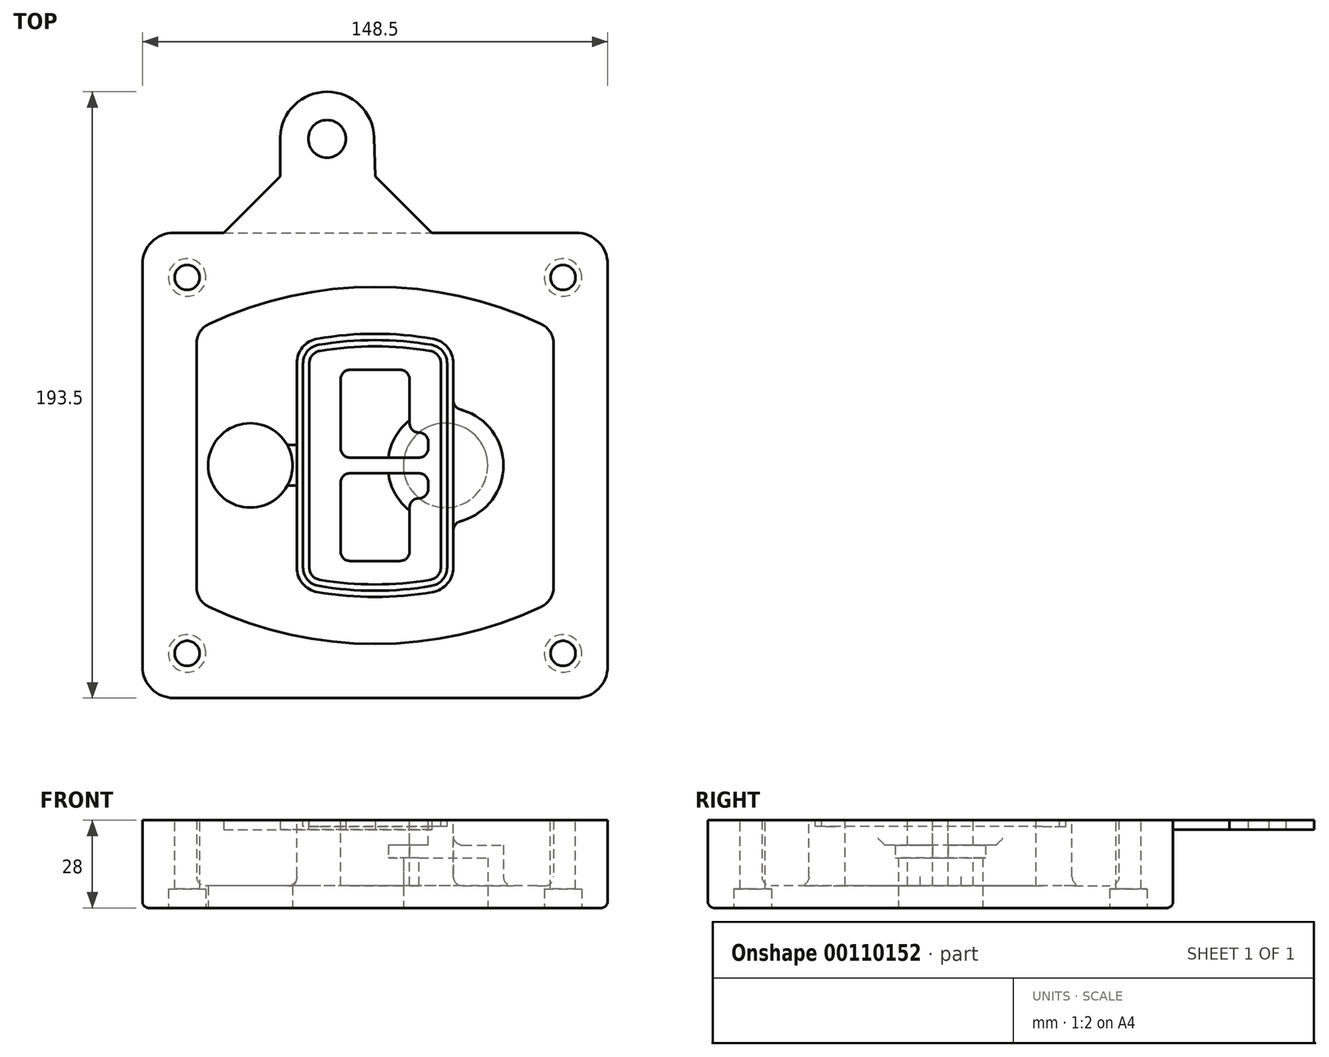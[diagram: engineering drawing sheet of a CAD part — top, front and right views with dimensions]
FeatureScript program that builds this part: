
annotation { "Feature Type Name" : "Feature", "Feature Type Description" : "" }
export const myFeature = defineFeature(function(context is Context, id is Id, definition is map)
    precondition{}
    {
        {
            var Q0;
            Q0=qCreatedBy(makeId("Top.planeOp"),FACE);
            var sketch = newSketch(context, id + "F0", { "sketchPlane" : qUnion([Q0])});
            skPoint(sketch, "E0.rect.middle", {"position": v(0, 0) * mm});
            skLineSegment(sketch, "E1.bottom", {"start": v(-64.25, -74.25) * mm, "end": v(64.25, -74.25) * mm});
            skLineSegment(sketch, "E1.top", {"start": v(-64.25, 74.25) * mm, "end": v(64.25, 74.25) * mm});
            skLineSegment(sketch, "E1.left", {"start": v(-74.25, -64.25) * mm, "end": v(-74.25, 64.25) * mm});
            skLineSegment(sketch, "E1.right", {"start": v(74.25, -64.25) * mm, "end": v(74.25, 64.25) * mm});
            skLineSegment(sketch, "E2", {"start": v(-74.25, 74.25) * mm, "end": v(74.25, -74.25) * mm, "construction": true});
            skLineSegment(sketch, "E3", {"start": v(74.25, 74.25) * mm, "end": v(-74.25, -74.25) * mm, "construction": true});
            skCircle(sketch, "E4", {"center": v(-60, 60) * mm, "radius": 4 * mm});
            skCircle(sketch, "E5", {"center": v(60, 60) * mm, "radius": 4 * mm});
            skCircle(sketch, "E6", {"center": v(60, -60) * mm, "radius": 4 * mm});
            skCircle(sketch, "E7", {"center": v(-60, -60) * mm, "radius": 4 * mm});
            skLineSegment(sketch, "E8", {"start": v(-60, 60) * mm, "end": v(60, 60) * mm, "construction": true});
            skLineSegment(sketch, "E9", {"start": v(60, 60) * mm, "end": v(60, -60) * mm, "construction": true});
            skLineSegment(sketch, "E10", {"start": v(60, -60) * mm, "end": v(-60, -60) * mm, "construction": true});
            skLineSegment(sketch, "E11", {"start": v(-60, -60) * mm, "end": v(-60, 60) * mm, "construction": true});
            skLineSegment(sketch, "E12", {"start": v(-60, 38.83) * mm, "end": v(-60, -38.83) * mm});
            skLineSegment(sketch, "E13", {"start": v(60, 38.83) * mm, "end": v(60, -38.83) * mm});
            skArc(sketch, "E14", {"start": v(54.26, 47.88) * mm, "mid": v(0, 60) * mm, "end": v(-54.26, 47.88) * mm});
            skArc(sketch, "E15", {"start": v(-54.26, -47.88) * mm, "mid": v(0, -60) * mm, "end": v(54.26, -47.88) * mm});
            skLineSegment(sketch, "E16", {"start": v(-60, 0) * mm, "end": v(60, 0) * mm, "construction": true});
            skPoint(sketch, "E17.visualSharp", {"position": v(-60, -45) * mm});
            skArc(sketch, "E17.filletArc", {"start": v(-60, -38.83) * mm, "mid": v(-58.44, -44.2) * mm, "end": v(-54.26, -47.88) * mm});
            skPoint(sketch, "E18.visualSharp", {"position": v(-60, 45) * mm});
            skArc(sketch, "E18.filletArc", {"start": v(-54.26, 47.88) * mm, "mid": v(-58.44, 44.2) * mm, "end": v(-60, 38.83) * mm});
            skPoint(sketch, "E19.visualSharp", {"position": v(60, 45) * mm});
            skArc(sketch, "E19.filletArc", {"start": v(60, 38.83) * mm, "mid": v(58.44, 44.2) * mm, "end": v(54.26, 47.88) * mm});
            skPoint(sketch, "E20.visualSharp", {"position": v(60, -45) * mm});
            skArc(sketch, "E20.filletArc", {"start": v(54.26, -47.88) * mm, "mid": v(58.44, -44.2) * mm, "end": v(60, -38.83) * mm});
            skPoint(sketch, "E21.visualSharp", {"position": v(-74.25, 74.25) * mm});
            skArc(sketch, "E21.filletArc", {"start": v(-64.25, 74.25) * mm, "mid": v(-71.32, 71.32) * mm, "end": v(-74.25, 64.25) * mm});
            skPoint(sketch, "E22.visualSharp", {"position": v(74.25, 74.25) * mm});
            skArc(sketch, "E22.filletArc", {"start": v(74.25, 64.25) * mm, "mid": v(71.32, 71.32) * mm, "end": v(64.25, 74.25) * mm});
            skPoint(sketch, "E23.visualSharp", {"position": v(74.25, -74.25) * mm});
            skArc(sketch, "E23.filletArc", {"start": v(64.25, -74.25) * mm, "mid": v(71.32, -71.32) * mm, "end": v(74.25, -64.25) * mm});
            skPoint(sketch, "E24.visualSharp", {"position": v(-74.25, -74.25) * mm});
            skArc(sketch, "E24.filletArc", {"start": v(-74.25, -64.25) * mm, "mid": v(-71.32, -71.32) * mm, "end": v(-64.25, -74.25) * mm});
            skArc(sketch, "E25.0", {"start": v(57, 38.83) * mm, "mid": v(55.9, 42.58) * mm, "end": v(52.98, 45.17) * mm});
            skLineSegment(sketch, "E25.1", {"start": v(57, 38.83) * mm, "end": v(57, -38.83) * mm});
            skArc(sketch, "E25.2", {"start": v(52.98, -45.17) * mm, "mid": v(55.9, -42.58) * mm, "end": v(57, -38.83) * mm});
            skArc(sketch, "E25.3", {"start": v(-52.98, -45.17) * mm, "mid": v(0, -57) * mm, "end": v(52.98, -45.17) * mm});
            skArc(sketch, "E25.4", {"start": v(-57, -38.83) * mm, "mid": v(-55.9, -42.58) * mm, "end": v(-52.98, -45.17) * mm});
            skArc(sketch, "E25.5", {"start": v(52.98, 45.17) * mm, "mid": v(0, 57) * mm, "end": v(-52.98, 45.17) * mm});
            skLineSegment(sketch, "E25.6", {"start": v(-57, 38.83) * mm, "end": v(-57, -38.83) * mm});
            skArc(sketch, "E25.7", {"start": v(-52.98, 45.17) * mm, "mid": v(-55.9, 42.58) * mm, "end": v(-57, 38.83) * mm});
            skArc(sketch, "E26.0", {"start": v(-55.96, 51.5) * mm, "mid": v(-61.82, 46.33) * mm, "end": v(-64, 38.83) * mm});
            skArc(sketch, "E26.1", {"start": v(55.96, 51.5) * mm, "mid": v(0, 64) * mm, "end": v(-55.96, 51.5) * mm});
            skArc(sketch, "E26.2", {"start": v(64, 38.83) * mm, "mid": v(61.82, 46.33) * mm, "end": v(55.96, 51.5) * mm});
            skLineSegment(sketch, "E26.3", {"start": v(64, 38.83) * mm, "end": v(64, -38.83) * mm});
            skArc(sketch, "E26.4", {"start": v(55.96, -51.5) * mm, "mid": v(61.82, -46.33) * mm, "end": v(64, -38.83) * mm});
            skLineSegment(sketch, "E26.5", {"start": v(-64, 38.83) * mm, "end": v(-64, -38.83) * mm});
            skArc(sketch, "E26.6", {"start": v(-55.96, -51.5) * mm, "mid": v(0, -64) * mm, "end": v(55.96, -51.5) * mm});
            skArc(sketch, "E26.7", {"start": v(-64, -38.83) * mm, "mid": v(-61.82, -46.33) * mm, "end": v(-55.96, -51.5) * mm});
            skSolve(sketch);
        }
        {
            var Q0;
            Q0=makeQuery(id+"F0.imprint","IMPRINT",FACE,{"disambiguationData":[TD([[makeQuery(id+"F0.imprint","IMPRINT",EDGE,{"derivedFrom":sQuery(id+"F0.wireOp",EDGE,"E1.bottom")}),1.0]])]});
            var Q1;
            Q1=makeQuery(id+"F0.imprint","IMPRINT",FACE,{"disambiguationData":[TD([[makeQuery(id+"F0.imprint","IMPRINT",EDGE,{"derivedFrom":sQuery(id+"F0.wireOp",EDGE,"E12")}),1.0]])]});
            var Q2;
            Q2=makeQuery(id+"F0.imprint","IMPRINT",FACE,{"disambiguationData":[TD([[makeQuery(id+"F0.imprint","IMPRINT",EDGE,{"derivedFrom":sQuery(id+"F0.wireOp",EDGE,"E25.0")}),1.0]])]});
            var Q3;
            Q3=makeQuery(id+"F0.imprint","IMPRINT",FACE,{"disambiguationData":[TD([[makeQuery(id+"F0.imprint","IMPRINT",EDGE,{"derivedFrom":sQuery(id+"F0.wireOp",EDGE,"E12")}),-1.0]])]});
            extrude(context, id + "F1", {"entities" : qUnion([Q0, Q1, Q2, Q3]), "oppositeDirection" : true, "depth" : 25 * mm});
        }
        {
            var Q0;
            Q0=makeQuery(id+"F0.imprint","IMPRINT",FACE,{"disambiguationData":[TD([[makeQuery(id+"F0.imprint","IMPRINT",EDGE,{"derivedFrom":sQuery(id+"F0.wireOp",EDGE,"E12")}),1.0]])]});
            extrude(context, id + "F2", {"entities" : qUnion([Q0]), "operationType" : NewBodyOperationType.ADD, "depth" : 3 * mm});
        }
        {
            var Q0;
            Q0=makeQuery(id+"F0.imprint","IMPRINT",FACE,{"disambiguationData":[TD([[makeQuery(id+"F0.imprint","IMPRINT",EDGE,{"derivedFrom":sQuery(id+"F0.wireOp",EDGE,"E25.0")}),1.0]])]});
            extrude(context, id + "F3", {"entities" : qUnion([Q0]), "operationType" : NewBodyOperationType.REMOVE, "oppositeDirection" : true, "depth" : 18 * mm});
        }
        {
            var Q0;
            Q0=makeQuery(id+"F2.opExtrude","CAP_FACE",FACE,{"disambiguationData":[OSD([sQuery(id+"F0.wireOp",EDGE,"E12"),sQuery(id+"F0.wireOp",EDGE,"E13"),sQuery(id+"F0.wireOp",EDGE,"E14"),sQuery(id+"F0.wireOp",EDGE,"E15"),sQuery(id+"F0.wireOp",EDGE,"E17.filletArc"),sQuery(id+"F0.wireOp",EDGE,"E18.filletArc"),sQuery(id+"F0.wireOp",EDGE,"E19.filletArc"),sQuery(id+"F0.wireOp",EDGE,"E20.filletArc"),sQuery(id+"F0.wireOp",EDGE,"E25.0"),sQuery(id+"F0.wireOp",EDGE,"E25.1"),sQuery(id+"F0.wireOp",EDGE,"E25.2"),sQuery(id+"F0.wireOp",EDGE,"E25.3"),sQuery(id+"F0.wireOp",EDGE,"E25.4"),sQuery(id+"F0.wireOp",EDGE,"E25.5"),sQuery(id+"F0.wireOp",EDGE,"E25.6"),sQuery(id+"F0.wireOp",EDGE,"E25.7")])],"isStart":false});
            var sketch = newSketch(context, id + "F4", { "sketchPlane" : qUnion([Q0])});
            skArc(sketch, "E27.0", {"start": v(-18.34, -40.45) * mm, "mid": v(0, -42) * mm, "end": v(18.34, -40.45) * mm});
            skArc(sketch, "E28.0", {"start": v(18.34, 40.45) * mm, "mid": v(0, 42) * mm, "end": v(-18.34, 40.45) * mm});
            skLineSegment(sketch, "E29", {"start": v(-25, 32.57) * mm, "end": v(-25, -32.57) * mm});
            skLineSegment(sketch, "E30", {"start": v(25, 32.57) * mm, "end": v(25, -32.57) * mm});
            skLineSegment(sketch, "E31", {"start": v(-25, 39.1) * mm, "end": v(25, 39.1) * mm, "construction": true});
            skLineSegment(sketch, "E32", {"start": v(-25, -39.1) * mm, "end": v(25, -39.1) * mm, "construction": true});
            skPoint(sketch, "E33.visualSharp", {"position": v(-25, 39.1) * mm});
            skArc(sketch, "E33.filletArc", {"start": v(-18.34, 40.45) * mm, "mid": v(-23.11, 37.73) * mm, "end": v(-25, 32.57) * mm});
            skPoint(sketch, "E34.visualSharp", {"position": v(25, 39.1) * mm});
            skArc(sketch, "E34.filletArc", {"start": v(25, 32.57) * mm, "mid": v(23.11, 37.73) * mm, "end": v(18.34, 40.45) * mm});
            skPoint(sketch, "E35.visualSharp", {"position": v(25, -39.1) * mm});
            skArc(sketch, "E35.filletArc", {"start": v(18.34, -40.45) * mm, "mid": v(23.11, -37.73) * mm, "end": v(25, -32.57) * mm});
            skPoint(sketch, "E36.visualSharp", {"position": v(-25, -39.1) * mm});
            skArc(sketch, "E36.filletArc", {"start": v(-25, -32.57) * mm, "mid": v(-23.11, -37.73) * mm, "end": v(-18.34, -40.45) * mm});
            skArc(sketch, "E37.0", {"start": v(52.98, 45.17) * mm, "mid": v(0, 57) * mm, "end": v(-52.98, 45.17) * mm});
            skArc(sketch, "E37.1", {"start": v(-52.98, 45.17) * mm, "mid": v(-55.9, 42.58) * mm, "end": v(-57, 38.83) * mm});
            skLineSegment(sketch, "E37.2", {"start": v(-57, 38.83) * mm, "end": v(-57, -38.83) * mm});
            skArc(sketch, "E37.3", {"start": v(-57, -38.83) * mm, "mid": v(-55.9, -42.58) * mm, "end": v(-52.98, -45.17) * mm});
            skArc(sketch, "E37.4", {"start": v(-52.98, -45.17) * mm, "mid": v(0, -57) * mm, "end": v(52.98, -45.17) * mm});
            skArc(sketch, "E37.5", {"start": v(52.98, -45.17) * mm, "mid": v(55.9, -42.58) * mm, "end": v(57, -38.83) * mm});
            skLineSegment(sketch, "E37.6", {"start": v(57, 38.83) * mm, "end": v(57, -38.83) * mm});
            skArc(sketch, "E37.7", {"start": v(57, 38.83) * mm, "mid": v(55.9, 42.58) * mm, "end": v(52.98, 45.17) * mm});
            skLineSegment(sketch, "E38.0", {"start": v(23, 32.57) * mm, "end": v(23, -32.57) * mm});
            skArc(sketch, "E38.1", {"start": v(18, -38.48) * mm, "mid": v(21.58, -36.44) * mm, "end": v(23, -32.57) * mm});
            skArc(sketch, "E38.2", {"start": v(-18, -38.48) * mm, "mid": v(0, -40) * mm, "end": v(18, -38.48) * mm});
            skArc(sketch, "E38.3", {"start": v(-23, -32.57) * mm, "mid": v(-21.58, -36.44) * mm, "end": v(-18, -38.48) * mm});
            skLineSegment(sketch, "E38.4", {"start": v(-23, 32.57) * mm, "end": v(-23, -32.57) * mm});
            skArc(sketch, "E38.5", {"start": v(23, 32.57) * mm, "mid": v(21.58, 36.44) * mm, "end": v(18, 38.48) * mm});
            skArc(sketch, "E38.6", {"start": v(-18, 38.48) * mm, "mid": v(-21.58, 36.44) * mm, "end": v(-23, 32.57) * mm});
            skArc(sketch, "E38.7", {"start": v(18, 38.48) * mm, "mid": v(0, 40) * mm, "end": v(-18, 38.48) * mm});
            skArc(sketch, "E39.0", {"start": v(21, 32.57) * mm, "mid": v(20.06, 35.15) * mm, "end": v(17.67, 36.5) * mm});
            skLineSegment(sketch, "E39.1", {"start": v(21, 32.57) * mm, "end": v(21, -32.57) * mm});
            skArc(sketch, "E39.2", {"start": v(17.67, -36.5) * mm, "mid": v(20.06, -35.15) * mm, "end": v(21, -32.57) * mm});
            skArc(sketch, "E39.3", {"start": v(-17.67, -36.5) * mm, "mid": v(0, -38) * mm, "end": v(17.67, -36.5) * mm});
            skArc(sketch, "E39.4", {"start": v(-21, -32.57) * mm, "mid": v(-20.06, -35.15) * mm, "end": v(-17.67, -36.5) * mm});
            skArc(sketch, "E39.5", {"start": v(17.67, 36.5) * mm, "mid": v(0, 38) * mm, "end": v(-17.67, 36.5) * mm});
            skLineSegment(sketch, "E39.6", {"start": v(-21, 32.57) * mm, "end": v(-21, -32.57) * mm});
            skArc(sketch, "E39.7", {"start": v(-17.67, 36.5) * mm, "mid": v(-20.06, 35.15) * mm, "end": v(-21, 32.57) * mm});
            skLineSegment(sketch, "E40", {"start": v(-25, 0) * mm, "end": v(25, 0) * mm, "construction": true});
            skLineSegment(sketch, "E41", {"start": v(-11, 5.5) * mm, "end": v(-11, 27.5) * mm});
            skLineSegment(sketch, "E42", {"start": v(-8, 30.5) * mm, "end": v(8, 30.5) * mm});
            skLineSegment(sketch, "E43", {"start": v(11, 27.5) * mm, "end": v(11, 13.5) * mm});
            skLineSegment(sketch, "E44", {"start": v(14, 10.5) * mm, "end": v(14, 10.5) * mm});
            skLineSegment(sketch, "E45", {"start": v(17, 7.5) * mm, "end": v(17, 5.5) * mm});
            skLineSegment(sketch, "E46", {"start": v(14, 2.5) * mm, "end": v(-8, 2.5) * mm});
            skPoint(sketch, "E47.visualSharp", {"position": v(-11, 30.5) * mm});
            skArc(sketch, "E47.filletArc", {"start": v(-8, 30.5) * mm, "mid": v(-10.12, 29.62) * mm, "end": v(-11, 27.5) * mm});
            skPoint(sketch, "E48.visualSharp", {"position": v(11, 30.5) * mm});
            skArc(sketch, "E48.filletArc", {"start": v(11, 27.5) * mm, "mid": v(10.12, 29.62) * mm, "end": v(8, 30.5) * mm});
            skPoint(sketch, "E49.visualSharp", {"position": v(11, 10.5) * mm});
            skArc(sketch, "E49.filletArc", {"start": v(11, 13.5) * mm, "mid": v(11.88, 11.38) * mm, "end": v(14, 10.5) * mm});
            skPoint(sketch, "E50.visualSharp", {"position": v(17, 10.5) * mm});
            skArc(sketch, "E50.filletArc", {"start": v(17, 7.5) * mm, "mid": v(16.12, 9.62) * mm, "end": v(14, 10.5) * mm});
            skPoint(sketch, "E51.visualSharp", {"position": v(17, 2.5) * mm});
            skArc(sketch, "E51.filletArc", {"start": v(14, 2.5) * mm, "mid": v(16.12, 3.38) * mm, "end": v(17, 5.5) * mm});
            skPoint(sketch, "E52.visualSharp", {"position": v(-11, 2.5) * mm});
            skArc(sketch, "E52.filletArc", {"start": v(-11, 5.5) * mm, "mid": v(-10.12, 3.38) * mm, "end": v(-8, 2.5) * mm});
            skLineSegment(sketch, "E53.0.MirrorCS", {"start": v(14, -2.5) * mm, "end": v(-8, -2.5) * mm});
            skArc(sketch, "E54.0.MirrorCS", {"start": v(-11, -5.5) * mm, "mid": v(-10.12, -3.38) * mm, "end": v(-8, -2.5) * mm});
            skLineSegment(sketch, "E55.0.MirrorCS", {"start": v(-11, -5.5) * mm, "end": v(-11, -27.5) * mm});
            skArc(sketch, "E56.0.MirrorCS", {"start": v(-8, -30.5) * mm, "mid": v(-10.12, -29.62) * mm, "end": v(-11, -27.5) * mm});
            skLineSegment(sketch, "E57.0.MirrorCS", {"start": v(-8, -30.5) * mm, "end": v(8, -30.5) * mm});
            skArc(sketch, "E58.0.MirrorCS", {"start": v(11, -27.5) * mm, "mid": v(10.12, -29.62) * mm, "end": v(8, -30.5) * mm});
            skLineSegment(sketch, "E59.0.MirrorCS", {"start": v(11, -27.5) * mm, "end": v(11, -13.5) * mm});
            skArc(sketch, "E60.0.MirrorCS", {"start": v(11, -13.5) * mm, "mid": v(11.88, -11.38) * mm, "end": v(14, -10.5) * mm});
            skArc(sketch, "E61.0.MirrorCS", {"start": v(17, -7.5) * mm, "mid": v(16.12, -9.62) * mm, "end": v(14, -10.5) * mm});
            skLineSegment(sketch, "E62.0.MirrorCS", {"start": v(17, -7.5) * mm, "end": v(17, -5.5) * mm});
            skArc(sketch, "E63.0.MirrorCS", {"start": v(14, -2.5) * mm, "mid": v(16.12, -3.38) * mm, "end": v(17, -5.5) * mm});
            skSolve(sketch);
        }
        {
            var Q0;
            Q0=makeQuery(id+"F4.imprint","IMPRINT",FACE,{"disambiguationData":[TD([[makeQuery(id+"F4.imprint","IMPRINT",EDGE,{"derivedFrom":sQuery(id+"F4.wireOp",EDGE,"E27.0")}),1.0]])]});
            var Q1;
            Q1=makeQuery(id+"F4.imprint","IMPRINT",FACE,{"disambiguationData":[TD([[makeQuery(id+"F4.imprint","IMPRINT",EDGE,{"derivedFrom":sQuery(id+"F4.wireOp",EDGE,"E38.0")}),-1.0]])]});
            var Q2;
            Q2=makeQuery(id+"F4.imprint","IMPRINT",FACE,{"disambiguationData":[TD([[makeQuery(id+"F4.imprint","IMPRINT",EDGE,{"derivedFrom":sQuery(id+"F4.wireOp",EDGE,"E39.0")}),1.0]])]});
            extrude(context, id + "F5", {"entities" : qUnion([Q0, Q1, Q2]), "operationType" : NewBodyOperationType.ADD, "endBound" : BoundingType.UP_TO_NEXT, "oppositeDirection" : true, "depth" : 25 * mm});
        }
        {
            var Q0;
            Q0=makeQuery(id+"F4.imprint","IMPRINT",FACE,{"disambiguationData":[TD([[makeQuery(id+"F4.imprint","IMPRINT",EDGE,{"derivedFrom":sQuery(id+"F4.wireOp",EDGE,"E38.0")}),-1.0]])]});
            extrude(context, id + "F6", {"entities" : qUnion([Q0]), "operationType" : NewBodyOperationType.REMOVE, "oppositeDirection" : true, "depth" : 2 * mm});
        }
        {
            var Q0;
            Q0=makeQuery(id+"F1.opExtrude","CAP_FACE",FACE,{"disambiguationData":[OSD([sQuery(id+"F0.wireOp",EDGE,"E1.bottom"),sQuery(id+"F0.wireOp",EDGE,"E1.top"),sQuery(id+"F0.wireOp",EDGE,"E1.left"),sQuery(id+"F0.wireOp",EDGE,"E1.right"),sQuery(id+"F0.wireOp",EDGE,"E4"),sQuery(id+"F0.wireOp",EDGE,"E5"),sQuery(id+"F0.wireOp",EDGE,"E6"),sQuery(id+"F0.wireOp",EDGE,"E7"),sQuery(id+"F0.wireOp",EDGE,"E21.filletArc"),sQuery(id+"F0.wireOp",EDGE,"E22.filletArc"),sQuery(id+"F0.wireOp",EDGE,"E23.filletArc"),sQuery(id+"F0.wireOp",EDGE,"E24.filletArc")])],"isStart":false});
            var sketch = newSketch(context, id + "F7", { "sketchPlane" : qUnion([Q0])});
            skCircle(sketch, "E64", {"center": v(22.5, 0) * mm, "radius": 13.47 * mm});
            skCircle(sketch, "E65", {"center": v(-39.81, 0) * mm, "radius": 13.47 * mm});
            skLineSegment(sketch, "E66", {"start": v(74.25, 0) * mm, "end": v(-74.25, 0) * mm});
            skCircle(sketch, "E67", {"center": v(22.5, 0) * mm, "radius": 18.47 * mm});
            skCircle(sketch, "E68", {"center": v(60, -60) * mm, "radius": 6 * mm});
            skCircle(sketch, "E69", {"center": v(-60, -60) * mm, "radius": 6 * mm});
            skCircle(sketch, "E70", {"center": v(-60, 60) * mm, "radius": 6 * mm});
            skCircle(sketch, "E71", {"center": v(60, 60) * mm, "radius": 6 * mm});
            skSolve(sketch);
        }
        {
            var Q0;
            {var subQ1=sQuery(id+"F7.wireOp",EDGE,"E66");var subQ4=sQuery(id+"F7.wireOp",EDGE,"E64");var subQ6=makeQuery(id+"F7.imprint","INTERSECT",VERTEX,{"disambiguationData":[OD(0.0)],"derivedFrom":[subQ4,subQ1]});Q0=makeQuery(id+"F7.imprint","IMPRINT",FACE,{"disambiguationData":[TD([[makeQuery(id+"F7.imprint","IMPRINT",EDGE,{"disambiguationData":[TD([[subQ6,-1.0]])],"derivedFrom":subQ4}),-1.0]])]});}
            var Q1;
            {var subQ0=sQuery(id+"F7.wireOp",EDGE,"E66");var subQ1=sQuery(id+"F7.wireOp",EDGE,"E64");var subQ3=makeQuery(id+"F7.imprint","INTERSECT",VERTEX,{"disambiguationData":[OD(0.0)],"derivedFrom":[subQ1,subQ0]});Q1=makeQuery(id+"F7.imprint","IMPRINT",FACE,{"disambiguationData":[TD([[makeQuery(id+"F7.imprint","IMPRINT",EDGE,{"disambiguationData":[TD([[subQ3,-1.0]])],"derivedFrom":subQ1}),1.0]])]});}
            var Q2;
            {var subQ0=sQuery(id+"F7.wireOp",EDGE,"E66");var subQ1=sQuery(id+"F7.wireOp",EDGE,"E64");var subQ3=makeQuery(id+"F7.imprint","INTERSECT",VERTEX,{"disambiguationData":[OD(0.0)],"derivedFrom":[subQ1,subQ0]});Q2=makeQuery(id+"F7.imprint","IMPRINT",FACE,{"disambiguationData":[TD([[makeQuery(id+"F7.imprint","IMPRINT",EDGE,{"disambiguationData":[TD([[subQ3,1.0]])],"derivedFrom":subQ1}),1.0]])]});}
            var Q3;
            {var subQ1=sQuery(id+"F7.wireOp",EDGE,"E66");var subQ4=sQuery(id+"F7.wireOp",EDGE,"E64");var subQ6=makeQuery(id+"F7.imprint","INTERSECT",VERTEX,{"disambiguationData":[OD(0.0)],"derivedFrom":[subQ4,subQ1]});Q3=makeQuery(id+"F7.imprint","IMPRINT",FACE,{"disambiguationData":[TD([[makeQuery(id+"F7.imprint","IMPRINT",EDGE,{"disambiguationData":[TD([[subQ6,1.0]])],"derivedFrom":subQ4}),-1.0]])]});}
            extrude(context, id + "F8", {"entities" : qUnion([Q0, Q1, Q2, Q3]), "operationType" : NewBodyOperationType.ADD, "oppositeDirection" : true, "depth" : 20 * mm});
        }
        {
            var Q0;
            {var subQ0=sQuery(id+"F7.wireOp",EDGE,"E66");var subQ1=sQuery(id+"F7.wireOp",EDGE,"E64");var subQ3=makeQuery(id+"F7.imprint","INTERSECT",VERTEX,{"disambiguationData":[OD(0.0)],"derivedFrom":[subQ1,subQ0]});Q0=makeQuery(id+"F7.imprint","IMPRINT",FACE,{"disambiguationData":[TD([[makeQuery(id+"F7.imprint","IMPRINT",EDGE,{"disambiguationData":[TD([[subQ3,-1.0]])],"derivedFrom":subQ1}),1.0]])]});}
            var Q1;
            {var subQ0=sQuery(id+"F7.wireOp",EDGE,"E66");var subQ1=sQuery(id+"F7.wireOp",EDGE,"E64");var subQ3=makeQuery(id+"F7.imprint","INTERSECT",VERTEX,{"disambiguationData":[OD(0.0)],"derivedFrom":[subQ1,subQ0]});Q1=makeQuery(id+"F7.imprint","IMPRINT",FACE,{"disambiguationData":[TD([[makeQuery(id+"F7.imprint","IMPRINT",EDGE,{"disambiguationData":[TD([[subQ3,1.0]])],"derivedFrom":subQ1}),1.0]])]});}
            extrude(context, id + "F9", {"entities" : qUnion([Q0, Q1]), "operationType" : NewBodyOperationType.REMOVE, "oppositeDirection" : true, "depth" : 16 * mm});
        }
        {
            var Q0;
            {var subQ0=sQuery(id+"F7.wireOp",EDGE,"E66");var subQ1=sQuery(id+"F7.wireOp",EDGE,"E65");var subQ3=makeQuery(id+"F7.imprint","INTERSECT",VERTEX,{"disambiguationData":[OD(0.0)],"derivedFrom":[subQ1,subQ0]});Q0=makeQuery(id+"F7.imprint","IMPRINT",FACE,{"disambiguationData":[TD([[makeQuery(id+"F7.imprint","IMPRINT",EDGE,{"disambiguationData":[TD([[subQ3,-1.0]])],"derivedFrom":subQ1}),1.0]])]});}
            var Q1;
            {var subQ0=sQuery(id+"F7.wireOp",EDGE,"E66");var subQ1=sQuery(id+"F7.wireOp",EDGE,"E65");var subQ3=makeQuery(id+"F7.imprint","INTERSECT",VERTEX,{"disambiguationData":[OD(0.0)],"derivedFrom":[subQ1,subQ0]});Q1=makeQuery(id+"F7.imprint","IMPRINT",FACE,{"disambiguationData":[TD([[makeQuery(id+"F7.imprint","IMPRINT",EDGE,{"disambiguationData":[TD([[subQ3,1.0]])],"derivedFrom":subQ1}),1.0]])]});}
            extrude(context, id + "F10", {"entities" : qUnion([Q0, Q1]), "operationType" : NewBodyOperationType.REMOVE, "oppositeDirection" : true, "depth" : 25 * mm});
        }
        {
            var Q0;
            Q0=makeQuery(id+"F7.imprint","IMPRINT",FACE,{"disambiguationData":[TD([[makeQuery(id+"F7.imprint","IMPRINT",EDGE,{"derivedFrom":sQuery(id+"F7.wireOp",EDGE,"E68")}),1.0]])]});
            var Q1;
            Q1=makeQuery(id+"F7.imprint","IMPRINT",FACE,{"disambiguationData":[TD([[makeQuery(id+"F7.imprint","IMPRINT",EDGE,{"derivedFrom":makeQuery(id+"F1.opExtrude","CAP_EDGE",EDGE,{"disambiguationData":[OSD([sQuery(id+"F0.wireOp",EDGE,"E5")])],"isStart":false})}),-1.0]])]});
            var Q2;
            Q2=makeQuery(id+"F7.imprint","IMPRINT",FACE,{"disambiguationData":[TD([[makeQuery(id+"F7.imprint","IMPRINT",EDGE,{"derivedFrom":sQuery(id+"F7.wireOp",EDGE,"E69")}),1.0]])]});
            var Q3;
            Q3=makeQuery(id+"F7.imprint","IMPRINT",FACE,{"disambiguationData":[TD([[makeQuery(id+"F7.imprint","IMPRINT",EDGE,{"derivedFrom":makeQuery(id+"F1.opExtrude","CAP_EDGE",EDGE,{"disambiguationData":[OSD([sQuery(id+"F0.wireOp",EDGE,"E4")])],"isStart":false})}),-1.0]])]});
            var Q4;
            Q4=makeQuery(id+"F7.imprint","IMPRINT",FACE,{"disambiguationData":[TD([[makeQuery(id+"F7.imprint","IMPRINT",EDGE,{"derivedFrom":sQuery(id+"F7.wireOp",EDGE,"E70")}),1.0]])]});
            var Q5;
            Q5=makeQuery(id+"F7.imprint","IMPRINT",FACE,{"disambiguationData":[TD([[makeQuery(id+"F7.imprint","IMPRINT",EDGE,{"derivedFrom":makeQuery(id+"F1.opExtrude","CAP_EDGE",EDGE,{"disambiguationData":[OSD([sQuery(id+"F0.wireOp",EDGE,"E7")])],"isStart":false})}),-1.0]])]});
            var Q6;
            Q6=makeQuery(id+"F7.imprint","IMPRINT",FACE,{"disambiguationData":[TD([[makeQuery(id+"F7.imprint","IMPRINT",EDGE,{"derivedFrom":sQuery(id+"F7.wireOp",EDGE,"E71")}),1.0]])]});
            var Q7;
            Q7=makeQuery(id+"F7.imprint","IMPRINT",FACE,{"disambiguationData":[TD([[makeQuery(id+"F7.imprint","IMPRINT",EDGE,{"derivedFrom":makeQuery(id+"F1.opExtrude","CAP_EDGE",EDGE,{"disambiguationData":[OSD([sQuery(id+"F0.wireOp",EDGE,"E6")])],"isStart":false})}),-1.0]])]});
            extrude(context, id + "F11", {"entities" : qUnion([Q0, Q1, Q2, Q3, Q4, Q5, Q6, Q7]), "operationType" : NewBodyOperationType.REMOVE, "oppositeDirection" : true, "depth" : 6 * mm});
        }
        {
            var Q0;
            Q0=makeQuery(id+"F9.boolean.opBoolean","COPY",FACE,{"derivedFrom":makeQuery(id+"F9.opExtrude","CAP_FACE",FACE,{"disambiguationData":[OSD([sQuery(id+"F7.wireOp",EDGE,"E64")])],"isStart":false})});
            var sketch = newSketch(context, id + "F12", { "sketchPlane" : qUnion([Q0])});
            skArc(sketch, "E72.0", {"start": v(11, 14.45) * mm, "mid": v(6.45, 9.13) * mm, "end": v(4.2, 2.5) * mm});
            skArc(sketch, "E72.1", {"start": v(4.2, -2.5) * mm, "mid": v(6.45, -9.13) * mm, "end": v(11, -14.45) * mm});
            skLineSegment(sketch, "E73", {"start": v(4.2, -2.5) * mm, "end": v(14, -2.5) * mm});
            skLineSegment(sketch, "E74.0", {"start": v(14, 2.5) * mm, "end": v(4.2, 2.5) * mm});
            skArc(sketch, "E74.1", {"start": v(14, 2.5) * mm, "mid": v(16.12, 3.38) * mm, "end": v(17, 5.5) * mm});
            skLineSegment(sketch, "E74.2", {"start": v(17, 7.5) * mm, "end": v(17, 5.5) * mm});
            skArc(sketch, "E74.3", {"start": v(17, 7.5) * mm, "mid": v(16.12, 9.62) * mm, "end": v(14, 10.5) * mm});
            skArc(sketch, "E74.4", {"start": v(11, 13.5) * mm, "mid": v(11.88, 11.38) * mm, "end": v(14, 10.5) * mm});
            skLineSegment(sketch, "E74.5", {"start": v(11, 14.45) * mm, "end": v(11, 13.5) * mm});
            skLineSegment(sketch, "E74.7", {"start": v(14, -2.5) * mm, "end": v(4.2, -2.5) * mm});
            skArc(sketch, "E74.8", {"start": v(14, -2.5) * mm, "mid": v(16.12, -3.38) * mm, "end": v(17, -5.5) * mm});
            skLineSegment(sketch, "E74.9", {"start": v(17, -7.5) * mm, "end": v(17, -5.5) * mm});
            skArc(sketch, "E74.10", {"start": v(17, -7.5) * mm, "mid": v(16.12, -9.62) * mm, "end": v(14, -10.5) * mm});
            skArc(sketch, "E74.11", {"start": v(11, -13.5) * mm, "mid": v(11.88, -11.38) * mm, "end": v(14, -10.5) * mm});
            skLineSegment(sketch, "E74.12", {"start": v(11, -14.45) * mm, "end": v(11, -13.5) * mm});
            skPoint(sketch, "E75.orphan", {"position": v(11, -27.5) * mm});
            skPoint(sketch, "E76.orphan", {"position": v(-8, -2.5) * mm});
            skPoint(sketch, "E77.orphan", {"position": v(-8, 2.5) * mm});
            skPoint(sketch, "E78.orphan", {"position": v(11, 27.5) * mm});
            skSolve(sketch);
        }
        {
            var Q0;
            {var subQ7=sQuery(id+"F12.wireOp",EDGE,"E72.0");var subQ14=sQuery(id+"F12.wireOp",EDGE,"E72.1");var subQ16=sQuery(id+"F12.wireOp",EDGE,"E74.1");var subQ18=sQuery(id+"F12.wireOp",EDGE,"E74.8");Q0=qUnion([makeQuery(id+"F12.imprint","IMPRINT",FACE,{"disambiguationData":[TD([[makeQuery(id+"F12.imprint","IMPRINT",EDGE,{"derivedFrom":subQ7}),1.0]])]}),makeQuery(id+"F12.imprint","IMPRINT",FACE,{"disambiguationData":[TD([[makeQuery(id+"F12.imprint","IMPRINT",EDGE,{"derivedFrom":subQ14}),1.0]])]}),makeQuery(id+"F12.imprint","IMPRINT",FACE,{"disambiguationData":[TD([[makeQuery(id+"F12.imprint","IMPRINT",EDGE,{"derivedFrom":subQ16}),1.0]])]}),makeQuery(id+"F12.imprint","IMPRINT",FACE,{"disambiguationData":[TD([[makeQuery(id+"F12.imprint","IMPRINT",EDGE,{"derivedFrom":subQ18}),-1.0]])]})]);}
            var Q1;
            Q1=makeQuery(id+"F5.boolean.opBoolean","SPLIT",FACE,{"disambiguationData":[TD([makeQuery(id+"F5.opExtrude","SWEPT_FACE",FACE,{"disambiguationData":[OSD([sQuery(id+"F4.wireOp",EDGE,"E41")])]})])],"derivedFrom":makeQuery(id+"F3.boolean.opBoolean","COPY",FACE,{"derivedFrom":makeQuery(id+"F3.opExtrude","CAP_FACE",FACE,{"disambiguationData":[OSD([sQuery(id+"F0.wireOp",EDGE,"E25.0"),sQuery(id+"F0.wireOp",EDGE,"E25.1"),sQuery(id+"F0.wireOp",EDGE,"E25.2"),sQuery(id+"F0.wireOp",EDGE,"E25.3"),sQuery(id+"F0.wireOp",EDGE,"E25.4"),sQuery(id+"F0.wireOp",EDGE,"E25.5"),sQuery(id+"F0.wireOp",EDGE,"E25.6"),sQuery(id+"F0.wireOp",EDGE,"E25.7")])],"isStart":false})})});
            extrude(context, id + "F13", {"entities" : qUnion([Q0]), "operationType" : NewBodyOperationType.REMOVE, "endBound" : BoundingType.UP_TO_SURFACE, "endBoundEntityFace" : qUnion([Q1]), "depth" : 25 * mm});
        }
        {
            var Q0;
            Q0=makeQuery(id+"F3.boolean.opBoolean","COPY",EDGE,{"derivedFrom":makeQuery(id+"F3.opExtrude","CAP_EDGE",EDGE,{"disambiguationData":[OSD([sQuery(id+"F0.wireOp",EDGE,"E25.6")])],"isStart":false})});
            var Q1;
            Q1=makeQuery(id+"F8.boolean.opBoolean","INTERSECT",EDGE,{"derivedFrom":[makeQuery(id+"F5.opExtrude","SWEPT_FACE",FACE,{"disambiguationData":[OSD([sQuery(id+"F4.wireOp",EDGE,"E30")])]}),makeQuery(id+"F8.opExtrude","CAP_FACE",FACE,{"disambiguationData":[OSD([sQuery(id+"F7.wireOp",EDGE,"E67")])],"isStart":false})]});
            var Q2;
            Q2=makeQuery(id+"F8.boolean.opBoolean","INTERSECT",EDGE,{"disambiguationData":[OD(1.0)],"derivedFrom":[makeQuery(id+"F5.opExtrude","SWEPT_FACE",FACE,{"disambiguationData":[OSD([sQuery(id+"F4.wireOp",EDGE,"E30")])]}),makeQuery(id+"F8.opExtrude","SWEPT_FACE",FACE,{"disambiguationData":[OSD([sQuery(id+"F7.wireOp",EDGE,"E67")])]})]});
            var Q3;
            {var subQ0=sQuery(id+"F4.wireOp",EDGE,"E30");Q3=makeQuery(id+"F8.boolean.opBoolean","SPLIT",EDGE,{"disambiguationData":[TD([makeQuery(id+"F5.opExtrude","SWEPT_FACE",FACE,{"disambiguationData":[OSD([sQuery(id+"F4.wireOp",EDGE,"E35.filletArc")])]})])],"derivedFrom":makeQuery(id+"F5.opExtrude","CAP_EDGE",EDGE,{"disambiguationData":[OSD([subQ0])],"isStart":false})});}
            var Q4;
            {var subQ0=sQuery(id+"F0.wireOp",EDGE,"E25.7");var subQ1=sQuery(id+"F0.wireOp",EDGE,"E25.1");var subQ2=sQuery(id+"F0.wireOp",EDGE,"E25.6");var subQ3=sQuery(id+"F0.wireOp",EDGE,"E25.5");var subQ4=sQuery(id+"F0.wireOp",EDGE,"E25.4");var subQ5=sQuery(id+"F0.wireOp",EDGE,"E25.0");var subQ6=sQuery(id+"F0.wireOp",EDGE,"E25.2");var subQ7=sQuery(id+"F0.wireOp",EDGE,"E25.3");Q4=makeQuery(id+"F8.boolean.opBoolean","INTERSECT",EDGE,{"derivedFrom":[makeQuery(id+"F5.boolean.opBoolean","SPLIT",FACE,{"disambiguationData":[TD([makeQuery(id+"F2.opExtrude","SWEPT_FACE",FACE,{"disambiguationData":[OSD([subQ5])]})])],"derivedFrom":makeQuery(id+"F3.boolean.opBoolean","COPY",FACE,{"derivedFrom":makeQuery(id+"F3.opExtrude","CAP_FACE",FACE,{"disambiguationData":[OSD([subQ5,subQ1,subQ6,subQ7,subQ4,subQ3,subQ2,subQ0])],"isStart":false})})}),makeQuery(id+"F8.opExtrude","SWEPT_FACE",FACE,{"disambiguationData":[OSD([sQuery(id+"F7.wireOp",EDGE,"E67")])]})]});}
            var Q5;
            Q5=makeQuery(id+"F8.boolean.opBoolean","INTERSECT",EDGE,{"disambiguationData":[OD(0.0)],"derivedFrom":[makeQuery(id+"F5.opExtrude","SWEPT_FACE",FACE,{"disambiguationData":[OSD([sQuery(id+"F4.wireOp",EDGE,"E30")])]}),makeQuery(id+"F8.opExtrude","SWEPT_FACE",FACE,{"disambiguationData":[OSD([sQuery(id+"F7.wireOp",EDGE,"E67")])]})]});
            fillet(context, id + "F14", {"entities" : qUnion([Q0, Q1, Q2, Q3, Q4, Q5]), "radius" : 3 * mm, "tangentPropagation" : true, "allowEdgeOverflow" : false});
        }
        {
            var Q0;
            Q0=makeQuery(id+"F1.opExtrude","CAP_EDGE",EDGE,{"disambiguationData":[OSD([sQuery(id+"F0.wireOp",EDGE,"E1.bottom")])],"isStart":false});
            fillet(context, id + "F15", {"entities" : qUnion([Q0]), "radius" : 2 * mm, "tangentPropagation" : true, "allowEdgeOverflow" : false});
        }
        {
            var Q0;
            {var subQ0=sQuery(id+"F0.wireOp",EDGE,"E22.filletArc");var subQ1=sQuery(id+"F0.wireOp",EDGE,"E7");var subQ2=sQuery(id+"F0.wireOp",EDGE,"E6");var subQ3=sQuery(id+"F0.wireOp",EDGE,"E5");var subQ4=sQuery(id+"F0.wireOp",EDGE,"E4");var subQ5=sQuery(id+"F0.wireOp",EDGE,"E1.bottom");var subQ6=sQuery(id+"F0.wireOp",EDGE,"E21.filletArc");var subQ7=sQuery(id+"F0.wireOp",EDGE,"E1.top");var subQ8=sQuery(id+"F0.wireOp",EDGE,"E1.left");var subQ9=sQuery(id+"F0.wireOp",EDGE,"E1.right");var subQ10=sQuery(id+"F0.wireOp",EDGE,"E23.filletArc");var subQ11=sQuery(id+"F0.wireOp",EDGE,"E24.filletArc");Q0=makeQuery(id+"F2.boolean.opBoolean","SPLIT",FACE,{"disambiguationData":[TD([makeQuery(id+"F1.opExtrude","SWEPT_FACE",FACE,{"disambiguationData":[OSD([subQ5])]})])],"derivedFrom":makeQuery(id+"F1.opExtrude","CAP_FACE",FACE,{"disambiguationData":[OSD([subQ5,subQ7,subQ8,subQ9,subQ4,subQ3,subQ2,subQ1,subQ6,subQ0,subQ10,subQ11])],"isStart":true})});}
            var sketch = newSketch(context, id + "F16", { "sketchPlane" : qUnion([Q0])});
            skLineSegment(sketch, "E79", {"start": v(-48.3, 74.25) * mm, "end": v(-30.3, 92.25) * mm});
            skLineSegment(sketch, "E80", {"start": v(18.1, 74.25) * mm, "end": v(0.1, 92.25) * mm});
            skLineSegment(sketch, "E81", {"start": v(-30.3, 92.25) * mm, "end": v(-30.3, 104.75) * mm});
            skLineSegment(sketch, "E82", {"start": v(-0.32, 104.75) * mm, "end": v(0.1, 92.25) * mm});
            skArc(sketch, "E83", {"start": v(-0.32, 104.75) * mm, "mid": v(-15.31, 119.25) * mm, "end": v(-30.3, 104.75) * mm});
            skCircle(sketch, "E84", {"center": v(-15.31, 104.25) * mm, "radius": 6 * mm});
            skLineSegment(sketch, "E85", {"start": v(-15.31, 104.25) * mm, "end": v(-15.31, 74.25) * mm, "construction": true});
            skLineSegment(sketch, "E86", {"start": v(-48.3, 74.25) * mm, "end": v(-15.31, 74.25) * mm});
            skLineSegment(sketch, "E87", {"start": v(-74.25, 0) * mm, "end": v(74.25, 0) * mm, "construction": true});
            skArc(sketch, "E88.MirrorCS", {"start": v(-0.32, -104.75) * mm, "mid": v(-15.31, -119.25) * mm, "end": v(-30.3, -104.75) * mm});
            skCircle(sketch, "E89.MirrorC", {"center": v(-15.31, -104.25) * mm, "radius": 6 * mm});
            skLineSegment(sketch, "E90.MirrorCS", {"start": v(-30.3, -92.25) * mm, "end": v(-30.3, -104.75) * mm});
            skLineSegment(sketch, "E91.MirrorCS", {"start": v(-48.3, -74.25) * mm, "end": v(-30.3, -92.25) * mm});
            skLineSegment(sketch, "E92.MirrorCS", {"start": v(-15.31, -104.25) * mm, "end": v(-15.31, -74.25) * mm, "construction": true});
            skLineSegment(sketch, "E93.MirrorCS", {"start": v(18.1, -74.25) * mm, "end": v(0.1, -92.25) * mm});
            skLineSegment(sketch, "E94.MirrorCS", {"start": v(-0.32, -104.75) * mm, "end": v(0.1, -92.25) * mm});
            skSolve(sketch);
        }
        {
            var Q0;
            Q0=makeQuery(id+"F16.imprint","IMPRINT",FACE,{"disambiguationData":[TD([[makeQuery(id+"F16.imprint","IMPRINT",EDGE,{"derivedFrom":sQuery(id+"F16.wireOp",EDGE,"E79")}),-1.0]])]});
            var Q1;
            Q1=makeQuery(id+"F16.imprint","IMPRINT",FACE,{"disambiguationData":[TD([[makeQuery(id+"F16.imprint","IMPRINT",EDGE,{"derivedFrom":sQuery(id+"F16.wireOp",EDGE,"E88.MirrorCS")}),-1.0]])]});
            var Q2;
            {var subQ5=sQuery(id+"F16.wireOp",EDGE,"E86");Q2=makeQuery(id+"F16.imprint","IMPRINT",FACE,{"disambiguationData":[TD([[makeQuery(id+"F16.imprint","IMPRINT",EDGE,{"derivedFrom":subQ5}),-1.0]])]});}
            var Q3;
            Q3=makeQuery(id+"F2.opExtrude","CAP_FACE",FACE,{"disambiguationData":[OSD([sQuery(id+"F0.wireOp",EDGE,"E12"),sQuery(id+"F0.wireOp",EDGE,"E13"),sQuery(id+"F0.wireOp",EDGE,"E14"),sQuery(id+"F0.wireOp",EDGE,"E15"),sQuery(id+"F0.wireOp",EDGE,"E17.filletArc"),sQuery(id+"F0.wireOp",EDGE,"E18.filletArc"),sQuery(id+"F0.wireOp",EDGE,"E19.filletArc"),sQuery(id+"F0.wireOp",EDGE,"E20.filletArc"),sQuery(id+"F0.wireOp",EDGE,"E25.0"),sQuery(id+"F0.wireOp",EDGE,"E25.1"),sQuery(id+"F0.wireOp",EDGE,"E25.2"),sQuery(id+"F0.wireOp",EDGE,"E25.3"),sQuery(id+"F0.wireOp",EDGE,"E25.4"),sQuery(id+"F0.wireOp",EDGE,"E25.5"),sQuery(id+"F0.wireOp",EDGE,"E25.6"),sQuery(id+"F0.wireOp",EDGE,"E25.7")])],"isStart":false});
            extrude(context, id + "F17", {"entities" : qUnion([Q0, Q1, Q2]), "operationType" : NewBodyOperationType.ADD, "endBound" : BoundingType.UP_TO_SURFACE, "endBoundEntityFace" : qUnion([Q3]), "depth" : 25 * mm});
        }
    });
